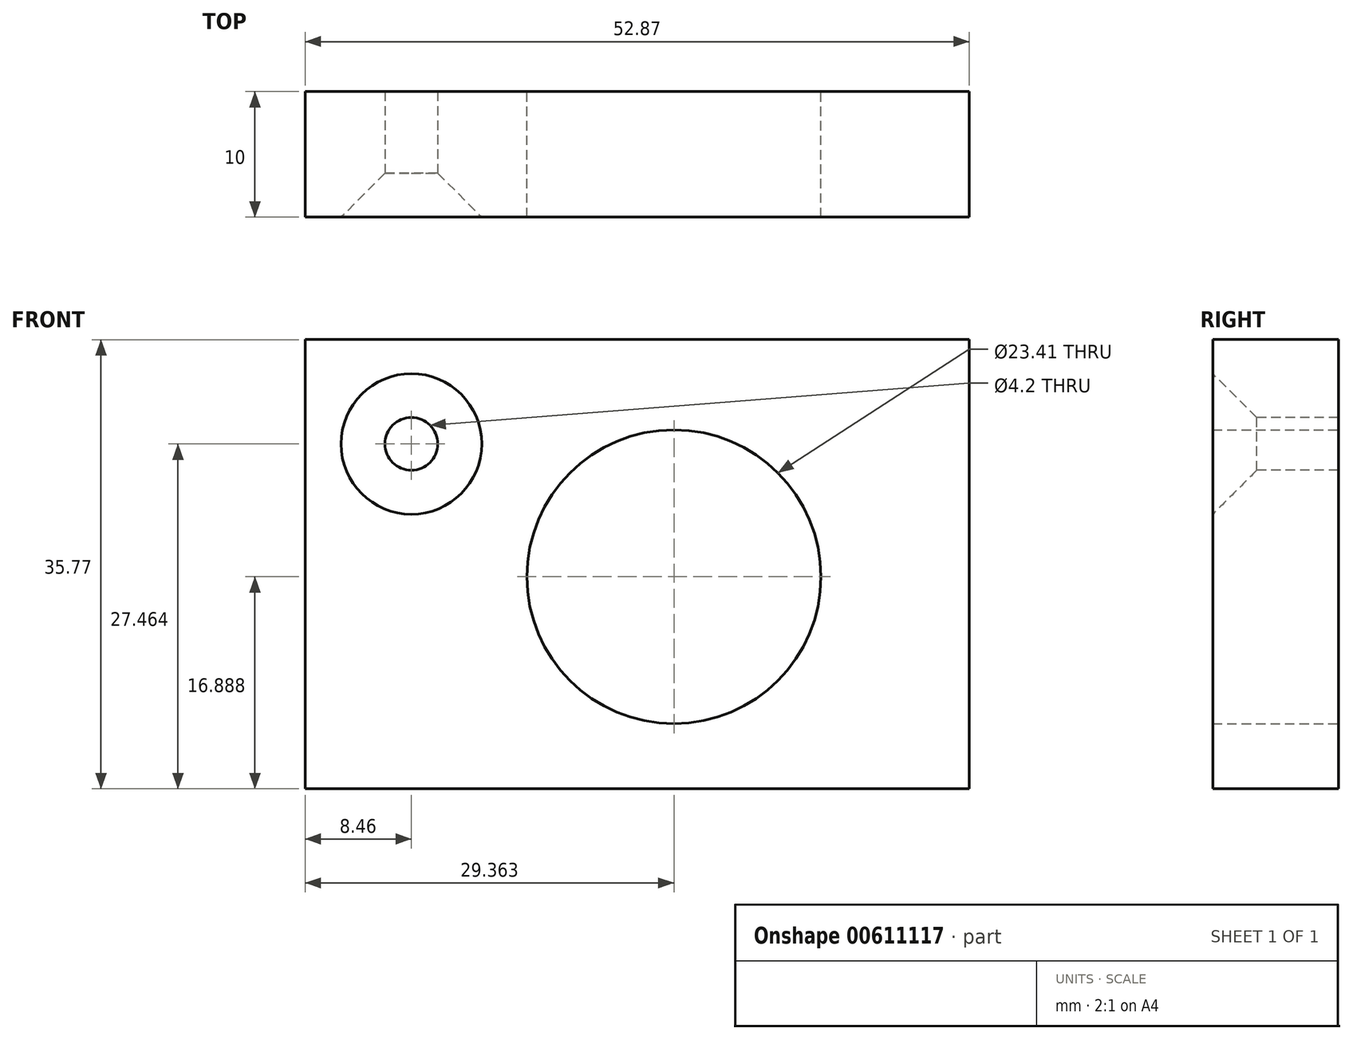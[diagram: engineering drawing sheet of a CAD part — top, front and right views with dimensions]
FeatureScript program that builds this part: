
annotation { "Feature Type Name" : "Feature", "Feature Type Description" : "" }
export const myFeature = defineFeature(function(context is Context, id is Id, definition is map)
    precondition{}
    {
        {
            var Q0;
            Q0=qCreatedBy(makeId("Front.planeOp"),FACE);
            var sketch = newSketch(context, id + "F0", { "sketchPlane" : qUnion([Q0])});
            skLineSegment(sketch, "E0.bottom", {"start": v(0, 0) * mm, "end": v(52.87, 0) * mm});
            skLineSegment(sketch, "E0.top", {"start": v(0, 35.77) * mm, "end": v(52.87, 35.77) * mm});
            skLineSegment(sketch, "E0.left", {"start": v(0, 0) * mm, "end": v(0, 35.77) * mm});
            skLineSegment(sketch, "E0.right", {"start": v(52.87, 0) * mm, "end": v(52.87, 35.77) * mm});
            skCircle(sketch, "E1", {"center": v(29.36, 16.89) * mm, "radius": 11.7 * mm});
            skSolve(sketch);
        }
        {
            var Q0;
            Q0=makeQuery(id+"F0.imprint","IMPRINT",FACE,{"disambiguationData":[TD([[makeQuery(id+"F0.imprint","IMPRINT",EDGE,{"derivedFrom":sQuery(id+"F0.wireOp",EDGE,"E0.bottom")}),1.0]])]});
            extrude(context, id + "F1", {"entities" : qUnion([Q0]), "endBound" : BoundingType.SYMMETRIC, "depth" : 10 * mm, "offsetDistance" : 25.4 * mm});
        }
        {
            var Q0;
            Q0=makeQuery(id+"F1.opExtrude","CAP_FACE",FACE,{"disambiguationData":[OSD([sQuery(id+"F0.wireOp",EDGE,"E0.bottom"),sQuery(id+"F0.wireOp",EDGE,"E0.top"),sQuery(id+"F0.wireOp",EDGE,"E0.left"),sQuery(id+"F0.wireOp",EDGE,"E0.right"),sQuery(id+"F0.wireOp",EDGE,"E1")])],"isStart":false});
            var sketch = newSketch(context, id + "F2", { "sketchPlane" : qUnion([Q0])});
            skPoint(sketch, "E2", {"position": v(8.46, 27.46) * mm});
            skSolve(sketch);
        }
        {
            var Q0;
            Q0=sQuery(id+"F2.wireOp",VERTEX,"E2");
            var Q1;
            Q1=makeQuery(id+"F1.opExtrude","SWEPT_BODY",BODY,{"disambiguationData":[OSD([sQuery(id+"F0.wireOp",EDGE,"E0.bottom"),sQuery(id+"F0.wireOp",EDGE,"E0.top"),sQuery(id+"F0.wireOp",EDGE,"E0.left"),sQuery(id+"F0.wireOp",EDGE,"E0.right"),sQuery(id+"F0.wireOp",EDGE,"E1")])]});
            hole(context, id + "F3", {"style" : HoleStyle.C_SINK, "endStyle" : HoleEndStyle.THROUGH, "standardTappedOrClearance" : lookupTablePath({ "standard" : "ISO", "engagement" : "75%", "pitch" : "0.8 mm", "size" : "M5", "type" : "Tapped" }), "standardBlindInLast" : lookupTablePath({ "standard" : "ISO", "engagement" : "75%", "pitch" : "0.8 mm", "size" : "M5", "type" : "Tapped" }), "holeDiameter" : 4.2 * mm, "cSinkDiameter" : 11.2 * mm, "cSinkAngle" : 90 * degree, "majorDiameter" : 5 * mm, "showTappedDepth" : true, "isTappedThrough" : true, "tappedDepth" : 12 * mm, "tapClearance" : 3, "startFromSketch" : true, "locations" : qUnion([Q0]), "scope" : qUnion([Q1])});
        }
    });
